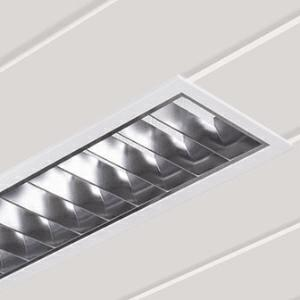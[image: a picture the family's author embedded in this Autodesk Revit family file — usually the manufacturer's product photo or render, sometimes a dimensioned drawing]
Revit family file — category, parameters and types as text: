
# Revit family: 3f_filippi_-_l_560_2s_3f_filippi_-_270935_-_l_561x30w_led_2s_221x1556
name_source: partatom
category: Lighting Fixtures
units: mm (PartAtom-declared; Revit-internal decimal feet)

## family parameters
Cut with Voids When Loaded = No
Host = Face
Light Source = No
Part Type = Normal
Room Calculation Point = No
Round Connector Dimension = Use Diameter
Shared = No

## types (1)
- 3F Filippi - L 560 2S (1 x LED, 3637 lm, 34 W, 4000 K)
    Apparent Load = 34 VA
    Approval mark = ENEC
    CIE Flux Codes = 78 98 100 100 100
    Color Rendering = 80
    Color Temperature = 4000 K
    Control Gear = Electronic ballast
    Default Elevation = 1800 mm
    Description = ILLUMINOTECHNICAL
Luminous efficiency 100% (DLOR 100%, ULOR 0%).
Initial luminous flux of the luminaire 3637 lm.
Direct symmetric distribution.
Installation Interdistance Transv.D = 0.99 x hu - Long.D = 1.04 x hu.
Average luminance <1000 cd/m² for radial angles >65°.
Tabular UGR (CIE 117 - 4H-8H; S=0.25H; 70/50/20): RUG 13.1 - 15.5.
Beam angle: 70° - 76°.
Luminous efficacy 107 lm/W.
Lifetime (L93/B10): 30000 h. (tq+25°C)
Lifetime (L90/B10): 50000 h. (tq+25°C)
Lifetime (L85/B10): 80000 h. (tq+25°C)
Lifetime (L80/B10): 100000 h. (tq+25°C)
Sudden decreased luminous flux after 50000 hours: 0% (C0).
Photobiological safety in compliance with IEC/TR 62778: RG0 risk exempt, (IEC 62471).
In compliance with IEC/EN 62722-2-1 - IEC/EN 62717 standards.

SOURCE
Linear LED module 30W/840.
Energy efficiency class (UE 2019/2020 - UE 2019/2015): D.
CIE 13.3 Colour rendering index: CRI >80 (R9 <50%).
IES TM-30 Fidelity Index: Rf = 84 Rg = 95.
CCT nominal colour temperature 4000 K.
Colour initial tolerance (MacAdam): SDCM 3.

MECHANICAL
Housing in galvannealed steel, painted in white epoxy-polyester.
2S parabolic louvre in semi-specular aluminium, non-reflecting, with transverse blades closed at the top.
Prismatic flat diffuser in transparent methacrylate (PMMA), multilenticular, anti-glare, prismatic exterior, placed above louvre blades.
Film protective against dust and finger marks, adhesive, attached to louvre.
Luminaire with limited surface temperature. - D - (EN 60598-2-24)
Dimensions: 1556x221 mm, height 95 mm. Weight 5.65 kg.
IP20 protection degree.
Mechanical strength to impacts IK02 (0.2 joule).
Glow-wire test resistance 650°C.

ELECTRICAL
Halogen Free electronic wiring 230V-50/60Hz, power factor 0.90, THD <25%, constant output current, SELV, class I, 1 driver.
Power of the luminaire 34 W.
CE - IEC 60598-1 - EN 60598-1.
SAFE FLICKER: PstLM=<1 and SVM=<0.4 (IEC TR 61547-1 and IEC TR 63158), to ensure a more comfortable and safe light.
Luminaire compliant with EN 60598-2-22 for power supply from a centralised emergency system CPSS (Central Power Supply System), not incorporated in the luminaire - high risk areas excluded. The default power and flux are 100% in AC and 100% in DC.
Ambient temperature from 0°C to +25°C.
Temperature class T6 max 85°C.
Relative humidity UR: <85%.

INSTALLATION
Pull-up recessed fitting / Slat ceiling recessed fitting.
False ceiling carving: 190x1530 mm.
All accessories dedicated to this product are available on the Catalog and on our website www.3F-Filippi.com.

APPLICATIONS
In environments with VDTs, managerial offices and staterooms, public offices and schools.

WARNING
Luminaire designed for disposal/recycling at end-of-life.
Replaceable (LED only) light source by a professional. Replaceable control gear by a professional.
    Height = 0 mm  [stored 0 ft]
    Lamp = 1 x LED
    Lamp Light Flux = 3637 lm
    Lamp Power = 34 W
    Lamp count = 1
    Length = 1556 mm
    Lifetime = 50000 h
    Luminous efficacy = 107 lm/W
    Manufacturer = 3F Filippi
    ModVariant = No
    Model = 3F Filippi - 270935 - L 561x30W LED 2S 221x1556
    Mounting Place = Ceiling
    Mounting Type = Recessed
    Number of Poles = 1
    OnlyDefault = Yes
    Power Factor = 1
    Product Name = 3F Filippi - L 560 2S
    Product group = recessed luminaire
    ProductGroupID = 4
    Protection Class = Protection class I
    Protection Degree = IP 20
    RLX_Detail_Level = 1
    RLX_Emergency_Light_Flux = 0 lm
    RLX_Emergency_Type = 0
    RLX_Emergency_Type_DB = No
    RlxData = <blob elided: 60937 chars, md5=429db0c5>
    Socket = socket
    Standby Power = 0 W
    System Light Flux = 3637 lm
    System Power = 34 W
    Type Comments = Product without accessories
    Type Image = 3ffilippi_270935.jpg
    URL = http://relux.com
    VarID = ---
    Voltage = 0 V
    Weight = 0.00 kg
    Width = 221 mm

note: [stored X ft] marks values corroborated as IEEE doubles in the binary element streams (Revit-internal decimal feet)

## geometry (parser evidence)
native form markers: Blend x4, Sweep x9
no freeform markers — native parametric forms only
